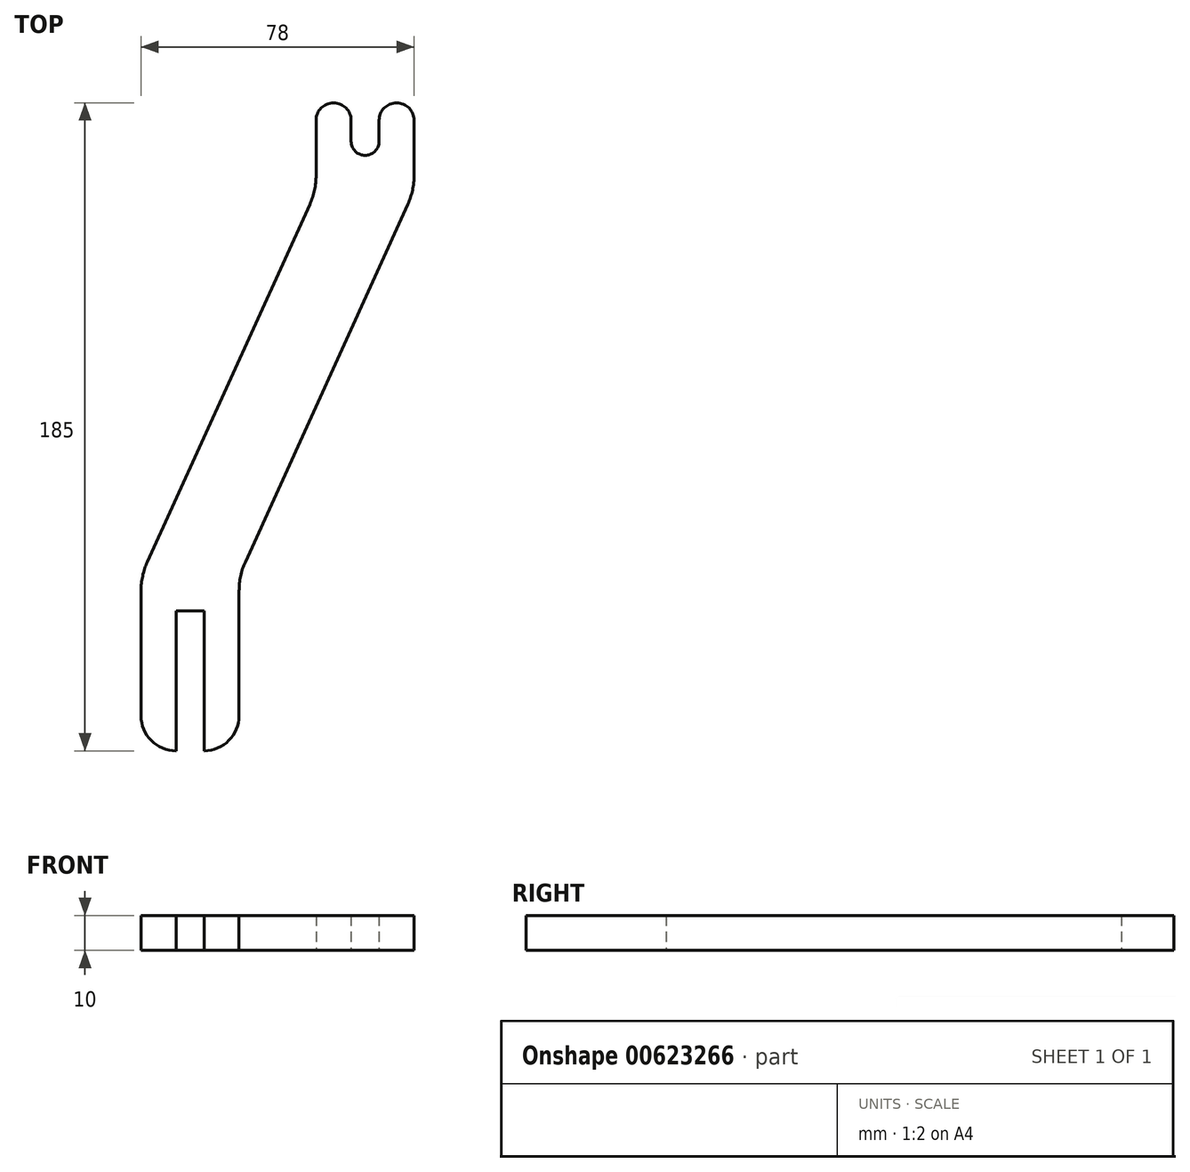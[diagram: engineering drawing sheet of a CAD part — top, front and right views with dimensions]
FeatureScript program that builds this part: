
annotation { "Feature Type Name" : "Feature", "Feature Type Description" : "" }
export const myFeature = defineFeature(function(context is Context, id is Id, definition is map)
    precondition{}
    {
        {
            var Q0;
            Q0=qCreatedBy(makeId("Top.planeOp"),FACE);
            var sketch = newSketch(context, id + "F0", { "sketchPlane" : qUnion([Q0])});
            skLineSegment(sketch, "E0", {"start": v(12.62, 61.4) * mm, "end": v(12.62, 77.06) * mm});
            skLineSegment(sketch, "E1", {"start": v(40.62, 77.06) * mm, "end": v(40.62, 61.4) * mm});
            skLineSegment(sketch, "E2", {"start": v(38.83, 53.12) * mm, "end": v(-7.59, -49) * mm});
            skLineSegment(sketch, "E3", {"start": v(-9.38, -57.27) * mm, "end": v(-9.38, -92.94) * mm});
            skLineSegment(sketch, "E4", {"start": v(-37.38, -92.94) * mm, "end": v(-37.38, -57.27) * mm});
            skLineSegment(sketch, "E5", {"start": v(-35.59, -49) * mm, "end": v(10.83, 53.12) * mm});
            skLineSegment(sketch, "E6", {"start": v(22.62, 77.06) * mm, "end": v(22.62, 71.06) * mm});
            skLineSegment(sketch, "E7", {"start": v(26.62, 67.06) * mm, "end": v(26.62, 67.06) * mm});
            skLineSegment(sketch, "E8", {"start": v(30.62, 71.06) * mm, "end": v(30.62, 77.06) * mm});
            skLineSegment(sketch, "E9", {"start": v(17.62, 82.06) * mm, "end": v(17.62, 82.06) * mm});
            skLineSegment(sketch, "E10", {"start": v(35.62, 82.06) * mm, "end": v(35.62, 82.06) * mm});
            skLineSegment(sketch, "E11", {"start": v(-27.38, -102.94) * mm, "end": v(-27.38, -102.94) * mm});
            skLineSegment(sketch, "E12", {"start": v(-27.38, -102.94) * mm, "end": v(-27.38, -62.94) * mm});
            skLineSegment(sketch, "E13", {"start": v(-27.38, -62.94) * mm, "end": v(-19.38, -62.94) * mm});
            skLineSegment(sketch, "E14", {"start": v(-19.38, -62.94) * mm, "end": v(-19.38, -102.94) * mm});
            skLineSegment(sketch, "E15", {"start": v(-19.38, -102.94) * mm, "end": v(-19.38, -102.94) * mm});
            skPoint(sketch, "E16.visualSharp", {"position": v(40.62, 57.06) * mm});
            skArc(sketch, "E16.filletArc", {"start": v(38.83, 53.12) * mm, "mid": v(40.17, 57.16) * mm, "end": v(40.62, 61.4) * mm});
            skPoint(sketch, "E17.visualSharp", {"position": v(12.62, 57.06) * mm});
            skArc(sketch, "E17.filletArc", {"start": v(10.83, 53.12) * mm, "mid": v(12.17, 57.16) * mm, "end": v(12.62, 61.4) * mm});
            skPoint(sketch, "E18.visualSharp", {"position": v(-9.38, -52.94) * mm});
            skArc(sketch, "E18.filletArc", {"start": v(-7.59, -49) * mm, "mid": v(-8.93, -53.04) * mm, "end": v(-9.38, -57.27) * mm});
            skPoint(sketch, "E19.visualSharp", {"position": v(-37.38, -52.94) * mm});
            skArc(sketch, "E19.filletArc", {"start": v(-35.59, -49) * mm, "mid": v(-36.93, -53.04) * mm, "end": v(-37.38, -57.27) * mm});
            skPoint(sketch, "E20.visualSharp", {"position": v(-37.38, -102.94) * mm});
            skArc(sketch, "E20.filletArc", {"start": v(-37.38, -92.94) * mm, "mid": v(-34.45, -100.01) * mm, "end": v(-27.38, -102.94) * mm});
            skPoint(sketch, "E21.visualSharp", {"position": v(-9.38, -102.94) * mm});
            skArc(sketch, "E21.filletArc", {"start": v(-19.38, -102.94) * mm, "mid": v(-12.31, -100.01) * mm, "end": v(-9.38, -92.94) * mm});
            skPoint(sketch, "E22.visualSharp", {"position": v(22.62, 82.06) * mm});
            skArc(sketch, "E22.filletArc", {"start": v(22.62, 77.06) * mm, "mid": v(21.15, 80.6) * mm, "end": v(17.62, 82.06) * mm});
            skPoint(sketch, "E23.visualSharp", {"position": v(12.62, 82.06) * mm});
            skArc(sketch, "E23.filletArc", {"start": v(17.62, 82.06) * mm, "mid": v(14.08, 80.6) * mm, "end": v(12.62, 77.06) * mm});
            skPoint(sketch, "E24.visualSharp", {"position": v(30.62, 82.06) * mm});
            skArc(sketch, "E24.filletArc", {"start": v(35.62, 82.06) * mm, "mid": v(32.08, 80.6) * mm, "end": v(30.62, 77.06) * mm});
            skPoint(sketch, "E25.visualSharp", {"position": v(40.62, 82.06) * mm});
            skArc(sketch, "E25.filletArc", {"start": v(40.62, 77.06) * mm, "mid": v(39.15, 80.6) * mm, "end": v(35.62, 82.06) * mm});
            skPoint(sketch, "E26.visualSharp", {"position": v(22.62, 67.06) * mm});
            skArc(sketch, "E26.filletArc", {"start": v(22.62, 71.06) * mm, "mid": v(23.79, 68.23) * mm, "end": v(26.62, 67.06) * mm});
            skPoint(sketch, "E27.visualSharp", {"position": v(30.62, 67.06) * mm});
            skArc(sketch, "E27.filletArc", {"start": v(26.62, 67.06) * mm, "mid": v(29.45, 68.23) * mm, "end": v(30.62, 71.06) * mm});
            skSolve(sketch);
        }
        {
            var Q0;
            Q0=makeQuery(id+"F0.imprint","IMPRINT",FACE,{"disambiguationData":[TD([[makeQuery(id+"F0.imprint","IMPRINT",EDGE,{"derivedFrom":sQuery(id+"F0.wireOp",EDGE,"E0")}),-1.0]])]});
            extrude(context, id + "F1", {"entities" : qUnion([Q0]), "depth" : 10 * mm, "offsetDistance" : 25 * mm});
        }
    });
